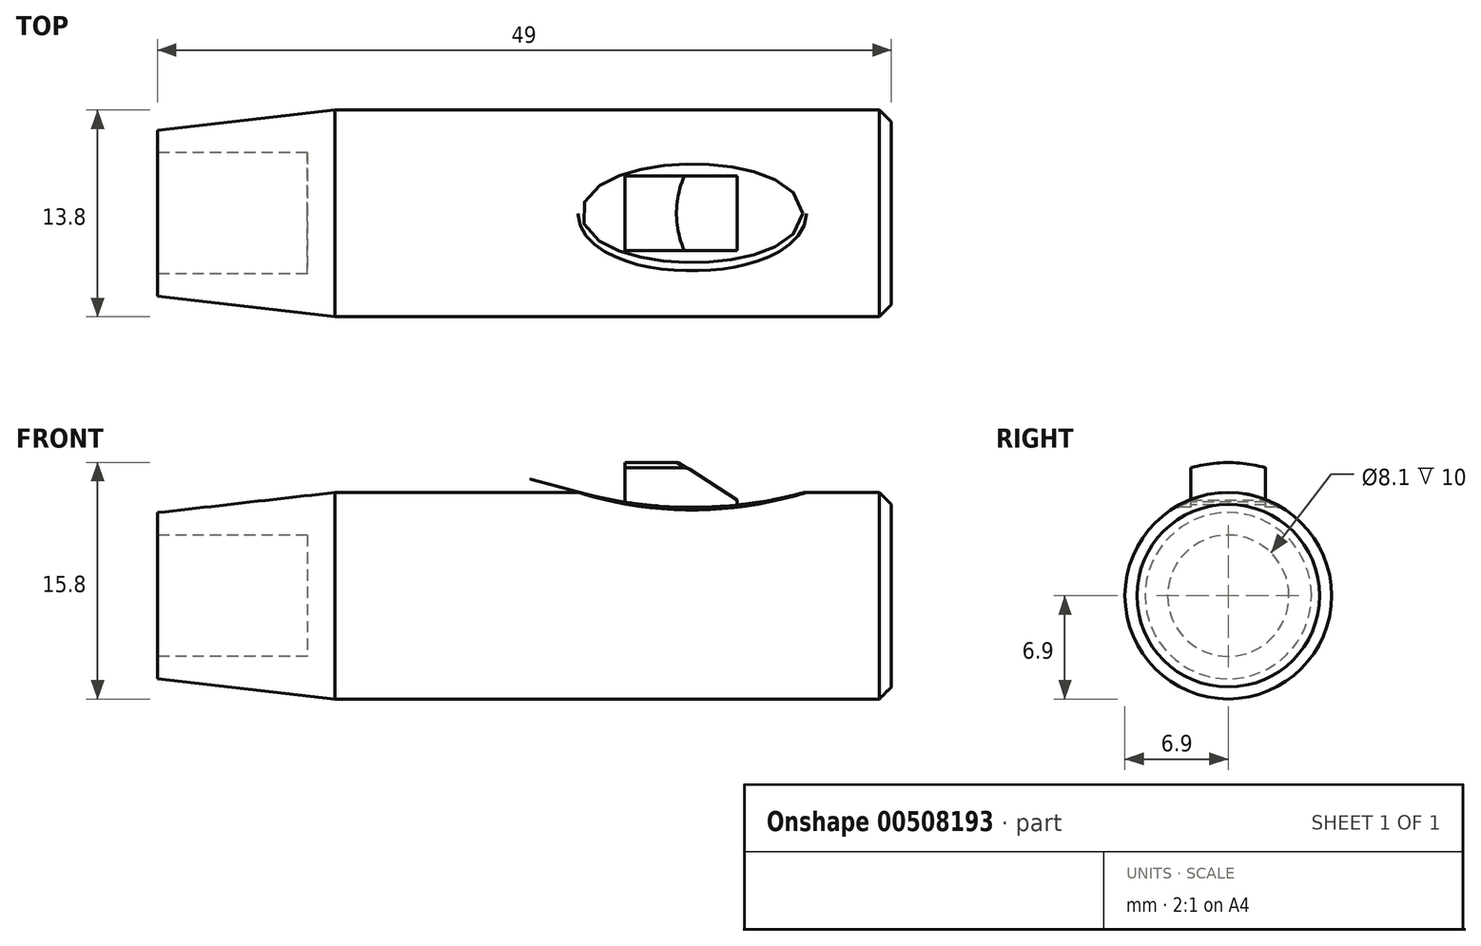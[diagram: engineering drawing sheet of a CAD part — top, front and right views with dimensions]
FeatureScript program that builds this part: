
annotation { "Feature Type Name" : "Feature", "Feature Type Description" : "" }
export const myFeature = defineFeature(function(context is Context, id is Id, definition is map)
    precondition{}
    {
        {
            var Q0;
            Q0=qCreatedBy(makeId("Front.planeOp"),FACE);
            var sketch = newSketch(context, id + "F0", { "sketchPlane" : qUnion([Q0])});
            skLineSegment(sketch, "E0", {"start": v(0, 0) * mm, "end": v(12, 0) * mm, "construction": true});
            skLineSegment(sketch, "E1", {"start": v(13, 4.55) * mm, "end": v(38, 7.4) * mm, "construction": true});
            skLineSegment(sketch, "E2", {"start": v(0, 4.95) * mm, "end": v(13, 4.95) * mm, "construction": true});
            skLineSegment(sketch, "E3", {"start": v(0, 4.95) * mm, "end": v(0, 8.4) * mm, "construction": true});
            skLineSegment(sketch, "E4", {"start": v(0, 8.4) * mm, "end": v(38, 8.4) * mm, "construction": true});
            skLineSegment(sketch, "E5", {"start": v(38, 8.4) * mm, "end": v(38, 7.4) * mm, "construction": true});
            skLineSegment(sketch, "E6.bottom", {"start": v(-6.75, 4.75) * mm, "end": v(12, 4.75) * mm, "construction": true});
            skLineSegment(sketch, "E6.top", {"start": v(-6.75, -4.75) * mm, "end": v(12, -4.75) * mm, "construction": true});
            skLineSegment(sketch, "E6.left", {"start": v(-6.75, 4.75) * mm, "end": v(-6.75, -4.75) * mm, "construction": true});
            skLineSegment(sketch, "E6.right", {"start": v(12, 4.75) * mm, "end": v(12, -4.75) * mm, "construction": true});
            skLineSegment(sketch, "E7", {"start": v(13, 4.95) * mm, "end": v(13, 4.55) * mm, "construction": true});
            skLineSegment(sketch, "E8.bottom", {"start": v(0, 4) * mm, "end": v(39.2, 4) * mm, "construction": true});
            skLineSegment(sketch, "E8.top", {"start": v(0, -4) * mm, "end": v(39.2, -4) * mm, "construction": true});
            skLineSegment(sketch, "E8.left", {"start": v(0, 4) * mm, "end": v(0, -4) * mm, "construction": true});
            skLineSegment(sketch, "E8.right", {"start": v(39.2, 4) * mm, "end": v(39.2, -4) * mm, "construction": true});
            skSolve(sketch);
        }
        {
            var Q0;
            Q0=qCreatedBy(makeId("Front.planeOp"),FACE);
            var sketch = newSketch(context, id + "F1", { "sketchPlane" : qUnion([Q0])});
            skLineSegment(sketch, "E9.0", {"start": v(21.77, 5.55) * mm, "end": v(33.61, 6.9) * mm});
            skLineSegment(sketch, "E10", {"start": v(33.61, 6.9) * mm, "end": v(70.77, 6.9) * mm});
            skLineSegment(sketch, "E11", {"start": v(70.77, 6.9) * mm, "end": v(70.77, 0) * mm});
            skLineSegment(sketch, "E12", {"start": v(70.77, 0) * mm, "end": v(31.77, 0) * mm});
            skLineSegment(sketch, "E13", {"start": v(21.77, 4.05) * mm, "end": v(31.77, 4.05) * mm});
            skLineSegment(sketch, "E14", {"start": v(31.77, 4.05) * mm, "end": v(31.77, 0) * mm});
            skLineSegment(sketch, "E15", {"start": v(21.77, 5.55) * mm, "end": v(21.77, 4.05) * mm});
            skPoint(sketch, "E16.orphan", {"position": v(38, 7.4) * mm});
            skSolve(sketch);
        }
        {
            var Q0;
            Q0=makeQuery(id+"F1.imprint","IMPRINT",FACE,{"disambiguationData":[TD([[makeQuery(id+"F1.imprint","IMPRINT",EDGE,{"derivedFrom":sQuery(id+"F1.wireOp",EDGE,"E9.0")}),-1.0]])]});
            var Q1;
            Q1=sQuery(id+"F0.wireOp",EDGE,"E0");
            revolve(context, id + "F2", {"surfaceOperationType" : NewSurfaceOperationType.NEW, "entities" : qUnion([Q0]), "axis" : qUnion([Q1]), "revolveType" : RevolveType.FULL});
        }
        {
            var Q0;
            Q0=qCreatedBy(makeId("Front.planeOp"),FACE);
            var sketch = newSketch(context, id + "F3", { "sketchPlane" : qUnion([Q0])});
            skLineSegment(sketch, "E17", {"start": v(52.97, 4.9) * mm, "end": v(60.47, 4.9) * mm});
            skLineSegment(sketch, "E18", {"start": v(60.47, 4.9) * mm, "end": v(60.47, 6.4) * mm});
            skLineSegment(sketch, "E19", {"start": v(60.47, 6.4) * mm, "end": v(56.57, 8.9) * mm});
            skLineSegment(sketch, "E20", {"start": v(56.57, 8.9) * mm, "end": v(52.97, 8.9) * mm});
            skLineSegment(sketch, "E21", {"start": v(52.97, 8.9) * mm, "end": v(52.97, 4.9) * mm});
            skArc(sketch, "E22", {"start": v(49.97, 6.9) * mm, "mid": v(57.47, 5.9) * mm, "end": v(64.97, 6.9) * mm});
            skLineSegment(sketch, "E23", {"start": v(49.97, 6.9) * mm, "end": v(64.97, 6.9) * mm});
            skSolve(sketch);
        }
        {
            var Q0;
            {var subQ3=sQuery(id+"F3.wireOp",EDGE,"E18");var subQ7=sQuery(id+"F3.wireOp",EDGE,"E19");var subQ8=makeQuery(id+"F3.imprint","INTERSECT",VERTEX,{"derivedFrom":[subQ3,subQ7]});Q0=makeQuery(id+"F3.imprint","IMPRINT",FACE,{"disambiguationData":[TD([[makeQuery(id+"F3.imprint","IMPRINT",EDGE,{"disambiguationData":[TD([[subQ8,1.0]])],"derivedFrom":subQ3}),1.0]])]});}
            var Q1;
            {var subQ0=sQuery(id+"F3.wireOp",EDGE,"E19");var subQ1=sQuery(id+"F3.wireOp",EDGE,"E18");var subQ2=makeQuery(id+"F3.imprint","INTERSECT",VERTEX,{"derivedFrom":[subQ1,subQ0]});Q1=makeQuery(id+"F3.imprint","IMPRINT",FACE,{"disambiguationData":[TD([[makeQuery(id+"F3.imprint","IMPRINT",EDGE,{"disambiguationData":[TD([[subQ2,1.0]])],"derivedFrom":subQ1}),-1.0]])]});}
            var Q2;
            {var subQ0=sQuery(id+"F3.wireOp",EDGE,"E22");var subQ1=sQuery(id+"F3.wireOp",EDGE,"E21");var subQ2=makeQuery(id+"F3.imprint","INTERSECT",VERTEX,{"derivedFrom":[subQ1,subQ0]});Q2=makeQuery(id+"F3.imprint","IMPRINT",FACE,{"disambiguationData":[TD([[makeQuery(id+"F3.imprint","IMPRINT",EDGE,{"disambiguationData":[TD([[subQ2,1.0]])],"derivedFrom":subQ1}),-1.0]])]});}
            extrude(context, id + "F4", {"entities" : qUnion([Q0, Q1, Q2]), "operationType" : NewBodyOperationType.REMOVE, "oppositeDirection" : true, "depth" : 25 * mm, "offsetDistance" : 25 * mm, "symmetric" : true});
        }
        {
            var Q0;
            Q0=makeQuery(id+"F4.boolean.opBoolean","INTERSECT",EDGE,{"derivedFrom":[makeQuery(id+"F2.opRevolve","SWEPT_FACE",FACE,{"disambiguationData":[OSD([sQuery(id+"F1.wireOp",EDGE,"E10")])]}),makeQuery(id+"F4.opExtrude","SWEPT_FACE",FACE,{"disambiguationData":[OSD([sQuery(id+"F3.wireOp",EDGE,"E22")])]})]});
            fillet(context, id + "F5", {"entities" : qUnion([Q0]), "tangentPropagation" : true, "radius" : 1 * mm, "defaultsChanged" : true, "vertexSettings" : [], "allowEdgeOverflow" : false});
        }
        {
            var Q0;
            {var subQ3=sQuery(id+"F3.wireOp",EDGE,"E20");Q0=makeQuery(id+"F3.imprint","IMPRINT",FACE,{"disambiguationData":[TD([[makeQuery(id+"F3.imprint","IMPRINT",EDGE,{"derivedFrom":subQ3}),1.0]])]});}
            var Q1;
            {var subQ3=sQuery(id+"F3.wireOp",EDGE,"E18");var subQ7=sQuery(id+"F3.wireOp",EDGE,"E19");var subQ8=makeQuery(id+"F3.imprint","INTERSECT",VERTEX,{"derivedFrom":[subQ3,subQ7]});Q1=makeQuery(id+"F3.imprint","IMPRINT",FACE,{"disambiguationData":[TD([[makeQuery(id+"F3.imprint","IMPRINT",EDGE,{"disambiguationData":[TD([[subQ8,1.0]])],"derivedFrom":subQ3}),1.0]])]});}
            var Q2;
            {var subQ0=sQuery(id+"F3.wireOp",EDGE,"E17");Q2=makeQuery(id+"F3.imprint","IMPRINT",FACE,{"disambiguationData":[TD([[makeQuery(id+"F3.imprint","IMPRINT",EDGE,{"derivedFrom":subQ0}),1.0]])]});}
            extrude(context, id + "F6", {"entities" : qUnion([Q0, Q1, Q2]), "operationType" : NewBodyOperationType.ADD, "depth" : 5 * mm, "offsetDistance" : 25 * mm, "symmetric" : true});
        }
        {
            var Q0;
            Q0=makeQuery(id+"F2.opRevolve","SWEPT_EDGE",EDGE,{"disambiguationData":[OSD([sQuery(id+"F1.wireOp",EDGE,"E10"),sQuery(id+"F1.wireOp",EDGE,"E11")])]});
            chamfer(context, id + "F7", {"entities" : qUnion([Q0]), "width" : 0.8 * mm, "tangentPropagation" : true});
        }
        {
            var Q0;
            Q0=makeQuery(id+"F6.opExtrude","SWEPT_FACE",FACE,{"disambiguationData":[OSD([sQuery(id+"F3.wireOp",EDGE,"E21")])]});
            var sketch = newSketch(context, id + "F8", { "sketchPlane" : qUnion([Q0])});
            skCircle(sketch, "E24", {"center": v(0, 0) * mm, "radius": 8.9 * mm});
            skCircle(sketch, "E25", {"center": v(0, 0) * mm, "radius": 9.24 * mm});
            skSolve(sketch);
        }
        {
            var Q0;
            Q0 = qSketchRegion(id + "F8", true);
            extrude(context, id + "F9", {"entities" : qUnion([Q0]), "operationType" : NewBodyOperationType.REMOVE, "endBound" : BoundingType.THROUGH_ALL, "oppositeDirection" : true, "depth" : 25 * mm, "offsetDistance" : 25 * mm});
        }
        {
            var Q0;
            Q0=makeQuery(id+"F9.boolean.opBoolean","INTERSECT",EDGE,{"derivedFrom":[makeQuery(id+"F6.opExtrude","SWEPT_FACE",FACE,{"disambiguationData":[OSD([sQuery(id+"F3.wireOp",EDGE,"E19")])]}),makeQuery(id+"F9.opExtrude","SWEPT_FACE",FACE,{"disambiguationData":[OSD([sQuery(id+"F8.wireOp",EDGE,"E24")])]})]});
            fillet(context, id + "F10", {"entities" : qUnion([Q0]), "tangentPropagation" : true, "radius" : 0.5 * mm, "defaultsChanged" : false, "vertexSettings" : [], "allowEdgeOverflow" : false});
        }
    });
